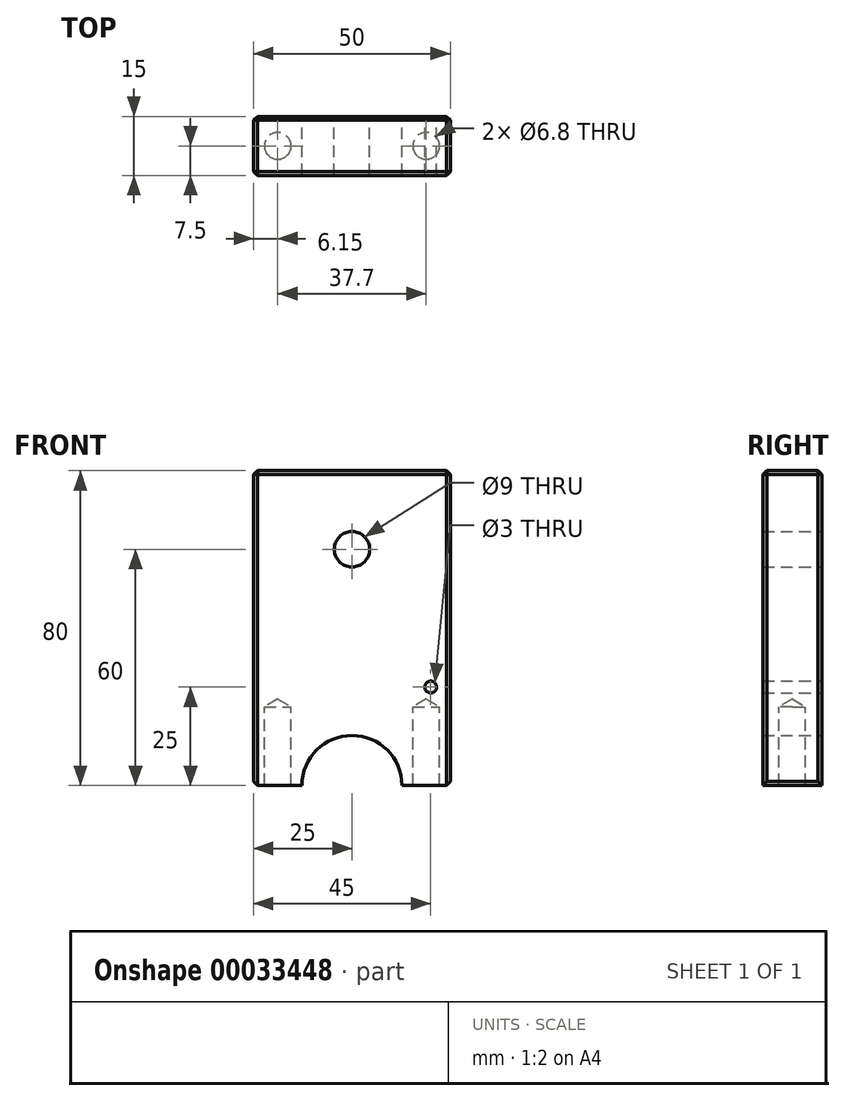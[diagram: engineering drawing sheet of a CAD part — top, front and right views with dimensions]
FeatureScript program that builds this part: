
annotation { "Feature Type Name" : "Feature", "Feature Type Description" : "" }
export const myFeature = defineFeature(function(context is Context, id is Id, definition is map)
    precondition{}
    {
        {
            var Q0;
            Q0=qCreatedBy(makeId("Front.planeOp"),FACE);
            var sketch = newSketch(context, id + "F0", { "sketchPlane" : qUnion([Q0])});
            skLineSegment(sketch, "E0.rect.bottom", {"start": v(-25, 40) * mm, "end": v(25, 40) * mm});
            skLineSegment(sketch, "E0.rect.top", {"start": v(-25, -40) * mm, "end": v(25, -40) * mm});
            skLineSegment(sketch, "E0.rect.left", {"start": v(-25, 40) * mm, "end": v(-25, -40) * mm});
            skLineSegment(sketch, "E0.rect.right", {"start": v(25, 40) * mm, "end": v(25, -40) * mm});
            skPoint(sketch, "E0.rect.middle", {"position": v(0, 0) * mm});
            skLineSegment(sketch, "E1", {"start": v(0, 49.3) * mm, "end": v(0, -50.45) * mm, "construction": true});
            skPoint(sketch, "E1.startSnap0", {"position": v(0, 40) * mm});
            skLineSegment(sketch, "E2.0", {"start": v(-25, -27.3) * mm, "end": v(15, -27.3) * mm, "construction": true});
            skLineSegment(sketch, "E3.0", {"start": v(-12.7, 49.3) * mm, "end": v(-12.7, -50.45) * mm, "construction": true});
            skLineSegment(sketch, "E4.0", {"start": v(12.7, 49.3) * mm, "end": v(12.7, -50.45) * mm, "construction": true});
            skArc(sketch, "E5", {"start": v(12.7, -40) * mm, "mid": v(0, -27.3) * mm, "end": v(-12.7, -40) * mm});
            skLineSegment(sketch, "E6.0", {"start": v(-20, 20) * mm, "end": v(20, 20) * mm, "construction": true});
            skLineSegment(sketch, "E7.0", {"start": v(-25, -20) * mm, "end": v(15, -20) * mm, "construction": true});
            skLineSegment(sketch, "E8.0", {"start": v(20, 40) * mm, "end": v(20, -40) * mm, "construction": true});
            skCircle(sketch, "E9", {"center": v(0, 20) * mm, "radius": 4.5 * mm});
            skPoint(sketch, "E10", {"position": v(20, -15) * mm});
            skCircle(sketch, "E11", {"center": v(20, -15) * mm, "radius": 1.5 * mm});
            skSolve(sketch);
        }
        {
            var Q0;
            Q0=makeQuery(id+"F0.imprint","IMPRINT",FACE,{"disambiguationData":[TD([[makeQuery(id+"F0.imprint","IMPRINT",EDGE,{"derivedFrom":sQuery(id+"F0.wireOp",EDGE,"E0.rect.bottom")}),-1.0]])]});
            extrude(context, id + "F1", {"entities" : qUnion([Q0]), "depth" : 15 * mm});
        }
        {
            var Q0;
            {var subQ0=sQuery(id+"F0.wireOp",EDGE,"E0.rect.top");Q0=makeQuery(id+"F1.opExtrude","SWEPT_FACE",FACE,{"disambiguationData":[OSD([subQ0]),TDD([makeQuery(id+"F0.imprint","IMPRINT",EDGE,{"disambiguationData":[TD([[makeQuery(id+"F0.imprint","INTERSECT",VERTEX,{"derivedFrom":[subQ0,sQuery(id+"F0.wireOp",EDGE,"E0.rect.left")]}),-1.0]])],"derivedFrom":subQ0})])]});}
            var sketch = newSketch(context, id + "F2", { "sketchPlane" : qUnion([Q0])});
            skLineSegment(sketch, "E12", {"start": v(-25, 15) * mm, "end": v(-12.7, 0) * mm, "construction": true});
            skLineSegment(sketch, "E13", {"start": v(-12.7, 15) * mm, "end": v(-25, 0) * mm, "construction": true});
            skPoint(sketch, "E14", {"position": v(-18.85, 7.5) * mm});
            skSolve(sketch);
        }
        {
            var Q0;
            Q0=sQuery(id+"F2.wireOp",VERTEX,"E14");
            var Q1;
            Q1=makeQuery(id+"F1.opExtrude","SWEPT_BODY",BODY,{"disambiguationData":[OSD([sQuery(id+"F0.wireOp",EDGE,"E0.rect.bottom"),sQuery(id+"F0.wireOp",EDGE,"E0.rect.top"),sQuery(id+"F0.wireOp",EDGE,"E0.rect.left"),sQuery(id+"F0.wireOp",EDGE,"E0.rect.right"),sQuery(id+"F0.wireOp",EDGE,"E5"),sQuery(id+"F0.wireOp",EDGE,"E9"),sQuery(id+"F0.wireOp",EDGE,"62824622-0037-4c73-98ec-75d92be364fd")])]});
            hole(context, id + "F3", {"style" : HoleStyle.SIMPLE, "holeDiameter" : 6.8 * mm, "endStyle" : HoleEndStyle.BLIND, "holeDepth" : 20 * mm, "locations" : qUnion([Q0]), "scope" : qUnion([Q1])});
        }
        {
            var Q0;
            {var subQ0=sQuery(id+"F0.wireOp",EDGE,"E0.rect.top");Q0=makeQuery(id+"F1.opExtrude","SWEPT_FACE",FACE,{"disambiguationData":[OSD([subQ0]),TDD([makeQuery(id+"F0.imprint","IMPRINT",EDGE,{"disambiguationData":[TD([[makeQuery(id+"F0.imprint","INTERSECT",VERTEX,{"derivedFrom":[subQ0,sQuery(id+"F0.wireOp",EDGE,"E0.rect.right")]}),1.0]])],"derivedFrom":subQ0})])]});}
            var sketch = newSketch(context, id + "F4", { "sketchPlane" : qUnion([Q0])});
            skLineSegment(sketch, "E15", {"start": v(12.7, 15) * mm, "end": v(25, 0) * mm, "construction": true});
            skLineSegment(sketch, "E16", {"start": v(25, 0) * mm, "end": v(25, 15) * mm, "construction": true});
            skLineSegment(sketch, "E17", {"start": v(25, 15) * mm, "end": v(12.7, 0) * mm, "construction": true});
            skPoint(sketch, "E18", {"position": v(18.85, 7.5) * mm});
            skSolve(sketch);
        }
        {
            var Q0;
            Q0=sQuery(id+"F4.wireOp",VERTEX,"E18");
            var Q1;
            Q1=makeQuery(id+"F1.opExtrude","SWEPT_BODY",BODY,{"disambiguationData":[OSD([sQuery(id+"F0.wireOp",EDGE,"E0.rect.bottom"),sQuery(id+"F0.wireOp",EDGE,"E0.rect.top"),sQuery(id+"F0.wireOp",EDGE,"E0.rect.left"),sQuery(id+"F0.wireOp",EDGE,"E0.rect.right"),sQuery(id+"F0.wireOp",EDGE,"E5"),sQuery(id+"F0.wireOp",EDGE,"E9"),sQuery(id+"F0.wireOp",EDGE,"62824622-0037-4c73-98ec-75d92be364fd")])]});
            hole(context, id + "F5", {"style" : HoleStyle.SIMPLE, "holeDiameter" : 6.8 * mm, "endStyle" : HoleEndStyle.BLIND, "holeDepth" : 20 * mm, "locations" : qUnion([Q0]), "scope" : qUnion([Q1])});
        }
        {
            var Q0;
            Q0=makeQuery(id+"F1.opExtrude","SWEPT_FACE",FACE,{"disambiguationData":[OSD([sQuery(id+"F0.wireOp",EDGE,"E0.rect.right")])]});
            var Q1;
            Q1=makeQuery(id+"F1.opExtrude","SWEPT_FACE",FACE,{"disambiguationData":[OSD([sQuery(id+"F0.wireOp",EDGE,"E0.rect.bottom")])]});
            var Q2;
            Q2=makeQuery(id+"F1.opExtrude","SWEPT_FACE",FACE,{"disambiguationData":[OSD([sQuery(id+"F0.wireOp",EDGE,"E0.rect.left")])]});
            chamfer(context, id + "F6", {"entities" : qUnion([Q0, Q1, Q2]), "width" : 1 * mm, "tangentPropagation" : true});
        }
    });
